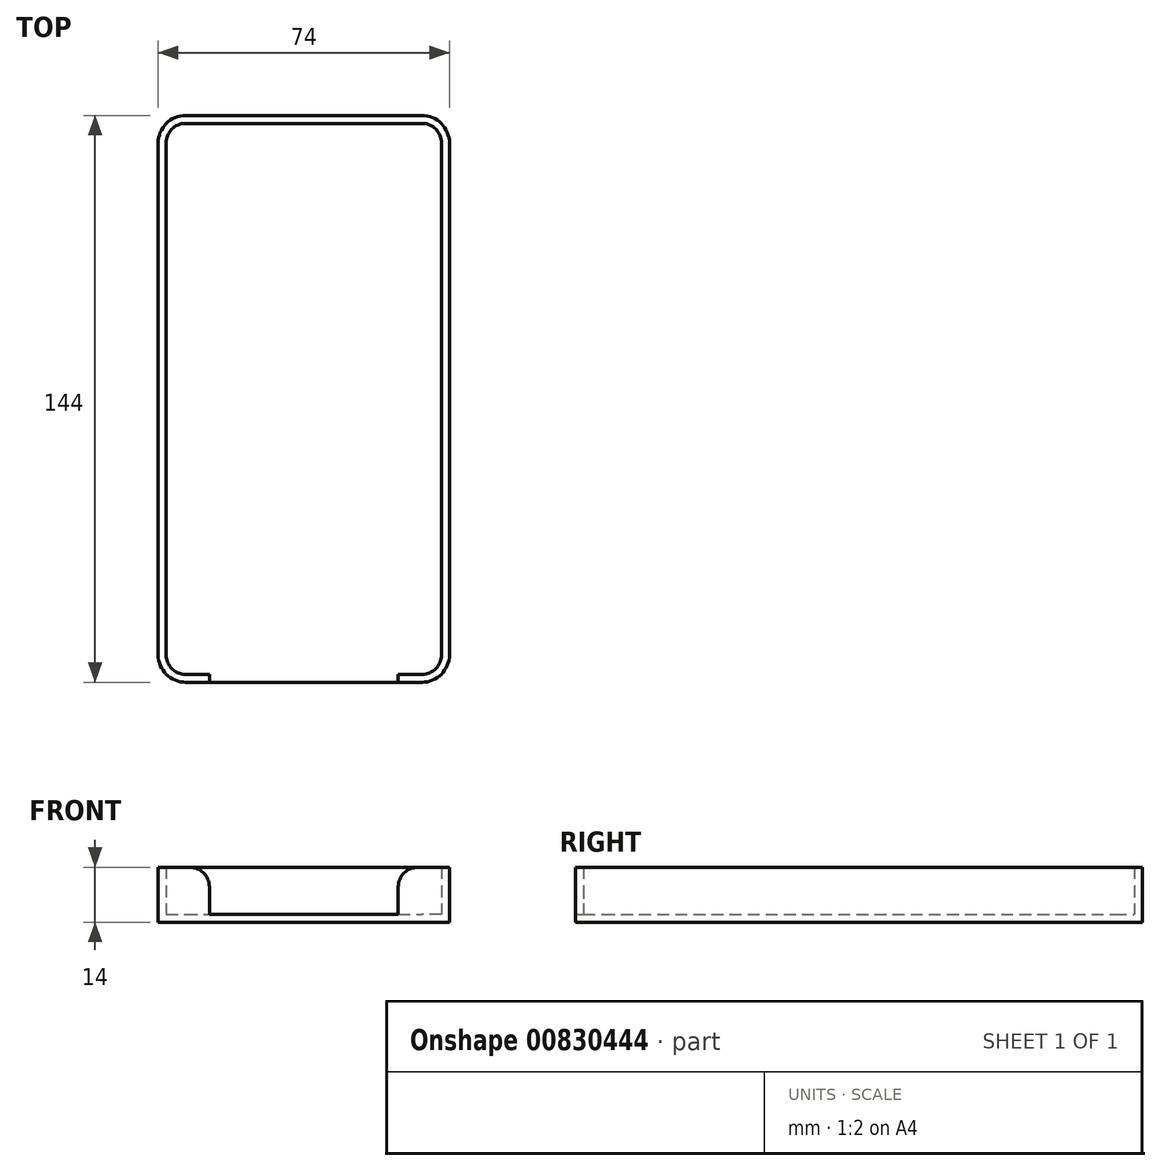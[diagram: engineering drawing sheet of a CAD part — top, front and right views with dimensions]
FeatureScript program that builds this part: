
annotation { "Feature Type Name" : "Feature", "Feature Type Description" : "" }
export const myFeature = defineFeature(function(context is Context, id is Id, definition is map)
    precondition{}
    {
        {
            var Q0;
            Q0=qCreatedBy(makeId("Top.planeOp"),FACE);
            var sketch = newSketch(context, id + "F0", { "sketchPlane" : qUnion([Q0])});
            skLineSegment(sketch, "E0.bottom", {"start": v(30, 70) * mm, "end": v(-30, 70) * mm});
            skLineSegment(sketch, "E0.top", {"start": v(30, -70) * mm, "end": v(-30, -70) * mm});
            skLineSegment(sketch, "E0.left", {"start": v(35, 65) * mm, "end": v(35, -65) * mm});
            skLineSegment(sketch, "E0.right", {"start": v(-35, 65) * mm, "end": v(-35, -65) * mm});
            skPoint(sketch, "E0.middle", {"position": v(0, 0) * mm});
            skPoint(sketch, "E1.visualSharp", {"position": v(-35, 70) * mm});
            skArc(sketch, "E1.filletArc", {"start": v(-30, 70) * mm, "mid": v(-33.54, 68.54) * mm, "end": v(-35, 65) * mm});
            skPoint(sketch, "E2.visualSharp", {"position": v(35, 70) * mm});
            skArc(sketch, "E2.filletArc", {"start": v(35, 65) * mm, "mid": v(33.54, 68.54) * mm, "end": v(30, 70) * mm});
            skPoint(sketch, "E3.visualSharp", {"position": v(35, -70) * mm});
            skArc(sketch, "E3.filletArc", {"start": v(30, -70) * mm, "mid": v(33.54, -68.54) * mm, "end": v(35, -65) * mm});
            skPoint(sketch, "E4.visualSharp", {"position": v(-35, -70) * mm});
            skArc(sketch, "E4.filletArc", {"start": v(-35, -65) * mm, "mid": v(-33.54, -68.54) * mm, "end": v(-30, -70) * mm});
            skLineSegment(sketch, "E5.0", {"start": v(30, 72) * mm, "end": v(-30, 72) * mm});
            skArc(sketch, "E5.1", {"start": v(37, 65) * mm, "mid": v(34.95, 69.95) * mm, "end": v(30, 72) * mm});
            skArc(sketch, "E5.2", {"start": v(-30, 72) * mm, "mid": v(-34.95, 69.95) * mm, "end": v(-37, 65) * mm});
            skLineSegment(sketch, "E5.3", {"start": v(37, 65) * mm, "end": v(37, -65) * mm});
            skLineSegment(sketch, "E5.4", {"start": v(-37, 65) * mm, "end": v(-37, -65) * mm});
            skArc(sketch, "E5.5", {"start": v(-37, -65) * mm, "mid": v(-34.95, -69.95) * mm, "end": v(-30, -72) * mm});
            skLineSegment(sketch, "E5.6", {"start": v(30, -72) * mm, "end": v(-30, -72) * mm});
            skArc(sketch, "E5.7", {"start": v(30, -72) * mm, "mid": v(34.95, -69.95) * mm, "end": v(37, -65) * mm});
            skSolve(sketch);
        }
        {
            var Q0;
            Q0 = qSketchRegion(id + "F0", true);
            var Q1;
            Q1=makeQuery(id+"F0.imprint","IMPRINT",FACE,{"disambiguationData":[TD([[makeQuery(id+"F0.imprint","IMPRINT",EDGE,{"derivedFrom":sQuery(id+"F0.wireOp",EDGE,"E0.bottom")}),1.0]])]});
            extrude(context, id + "F1", {"entities" : qUnion([Q0, Q1]), "depth" : 2 * mm, "offsetDistance" : 25 * mm});
        }
        {
            var Q0;
            Q0 = qSketchRegion(id + "F0", true);
            extrude(context, id + "F2", {"entities" : qUnion([Q0]), "operationType" : NewBodyOperationType.ADD, "depth" : 14 * mm, "offsetDistance" : 25 * mm});
        }
        {
            var Q0;
            Q0=makeQuery(id+"F1.opExtrude","CAP_FACE",FACE,{"disambiguationData":[OSD([sQuery(id+"F0.wireOp",EDGE,"E5.0"),sQuery(id+"F0.wireOp",EDGE,"E5.1"),sQuery(id+"F0.wireOp",EDGE,"E5.2"),sQuery(id+"F0.wireOp",EDGE,"E5.3"),sQuery(id+"F0.wireOp",EDGE,"E5.4"),sQuery(id+"F0.wireOp",EDGE,"E5.5"),sQuery(id+"F0.wireOp",EDGE,"E5.6"),sQuery(id+"F0.wireOp",EDGE,"E5.7")])],"isStart":false});
            var sketch = newSketch(context, id + "F3", { "sketchPlane" : qUnion([Q0])});
            skLineSegment(sketch, "E6.bottom", {"start": v(24, -77.94) * mm, "end": v(-24, -77.94) * mm});
            skLineSegment(sketch, "E6.top", {"start": v(24, -62.06) * mm, "end": v(-24, -62.06) * mm});
            skLineSegment(sketch, "E6.left", {"start": v(24, -77.94) * mm, "end": v(24, -62.06) * mm});
            skLineSegment(sketch, "E6.right", {"start": v(-24, -77.94) * mm, "end": v(-24, -62.06) * mm});
            skPoint(sketch, "E6.middle", {"position": v(0, -70) * mm});
            skSolve(sketch);
        }
        {
            var Q0;
            {var subQ0=sQuery(id+"F3.wireOp",EDGE,"E6.top");Q0=makeQuery(id+"F3.imprint","IMPRINT",FACE,{"disambiguationData":[TD([[makeQuery(id+"F3.imprint","IMPRINT",EDGE,{"derivedFrom":subQ0}),1.0]])]});}
            var Q1;
            {var subQ0=sQuery(id+"F3.wireOp",EDGE,"E6.bottom");Q1=makeQuery(id+"F3.imprint","IMPRINT",FACE,{"disambiguationData":[TD([[makeQuery(id+"F3.imprint","IMPRINT",EDGE,{"derivedFrom":subQ0}),-1.0]])]});}
            extrude(context, id + "F4", {"entities" : qUnion([Q0, Q1]), "operationType" : NewBodyOperationType.REMOVE, "depth" : 25 * mm, "offsetDistance" : 25 * mm});
        }
        {
            var Q0;
            Q0=makeQuery(id+"F4.boolean.opBoolean","INTERSECT",EDGE,{"derivedFrom":[makeQuery(id+"F2.opExtrude","CAP_FACE",FACE,{"disambiguationData":[OSD([sQuery(id+"F0.wireOp",EDGE,"E0.bottom"),sQuery(id+"F0.wireOp",EDGE,"E0.top"),sQuery(id+"F0.wireOp",EDGE,"E0.left"),sQuery(id+"F0.wireOp",EDGE,"E0.right"),sQuery(id+"F0.wireOp",EDGE,"E1.filletArc"),sQuery(id+"F0.wireOp",EDGE,"E2.filletArc"),sQuery(id+"F0.wireOp",EDGE,"E3.filletArc"),sQuery(id+"F0.wireOp",EDGE,"E4.filletArc"),sQuery(id+"F0.wireOp",EDGE,"E5.0"),sQuery(id+"F0.wireOp",EDGE,"E5.1"),sQuery(id+"F0.wireOp",EDGE,"E5.2"),sQuery(id+"F0.wireOp",EDGE,"E5.3"),sQuery(id+"F0.wireOp",EDGE,"E5.4"),sQuery(id+"F0.wireOp",EDGE,"E5.5"),sQuery(id+"F0.wireOp",EDGE,"E5.6"),sQuery(id+"F0.wireOp",EDGE,"E5.7")])],"isStart":false}),makeQuery(id+"F4.opExtrude","SWEPT_FACE",FACE,{"disambiguationData":[OSD([sQuery(id+"F3.wireOp",EDGE,"E6.right")])]})]});
            var Q1;
            Q1=makeQuery(id+"F4.boolean.opBoolean","INTERSECT",EDGE,{"derivedFrom":[makeQuery(id+"F2.opExtrude","CAP_FACE",FACE,{"disambiguationData":[OSD([sQuery(id+"F0.wireOp",EDGE,"E0.bottom"),sQuery(id+"F0.wireOp",EDGE,"E0.top"),sQuery(id+"F0.wireOp",EDGE,"E0.left"),sQuery(id+"F0.wireOp",EDGE,"E0.right"),sQuery(id+"F0.wireOp",EDGE,"E1.filletArc"),sQuery(id+"F0.wireOp",EDGE,"E2.filletArc"),sQuery(id+"F0.wireOp",EDGE,"E3.filletArc"),sQuery(id+"F0.wireOp",EDGE,"E4.filletArc"),sQuery(id+"F0.wireOp",EDGE,"E5.0"),sQuery(id+"F0.wireOp",EDGE,"E5.1"),sQuery(id+"F0.wireOp",EDGE,"E5.2"),sQuery(id+"F0.wireOp",EDGE,"E5.3"),sQuery(id+"F0.wireOp",EDGE,"E5.4"),sQuery(id+"F0.wireOp",EDGE,"E5.5"),sQuery(id+"F0.wireOp",EDGE,"E5.6"),sQuery(id+"F0.wireOp",EDGE,"E5.7")])],"isStart":false}),makeQuery(id+"F4.opExtrude","SWEPT_FACE",FACE,{"disambiguationData":[OSD([sQuery(id+"F3.wireOp",EDGE,"E6.left")])]})]});
            fillet(context, id + "F5", {"entities" : qUnion([Q0, Q1]), "radius" : 5 * mm, "tangentPropagation" : true, "allowEdgeOverflow" : false});
        }
    });
